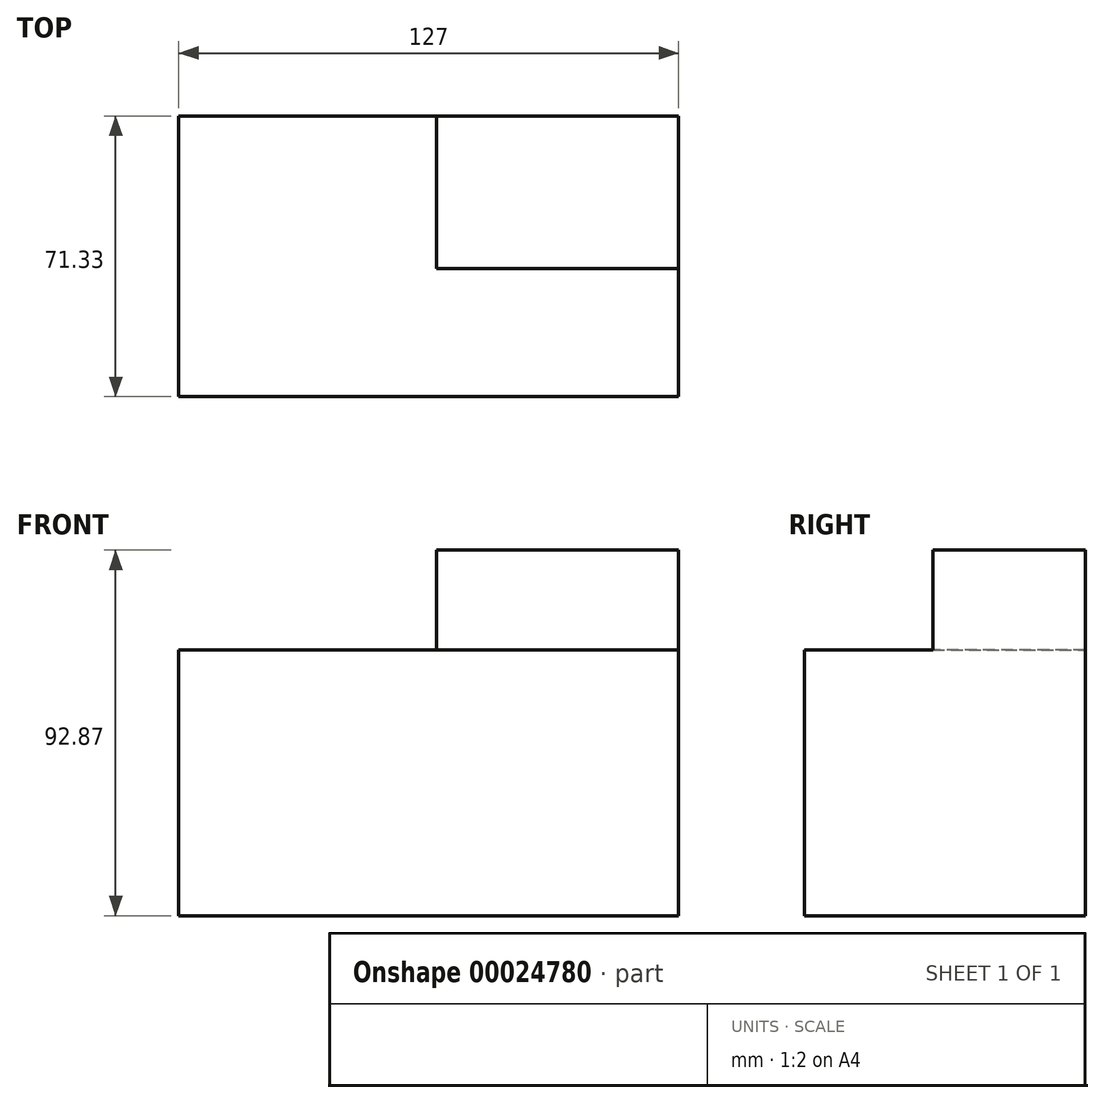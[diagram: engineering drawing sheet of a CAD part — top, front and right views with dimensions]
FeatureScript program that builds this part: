
annotation { "Feature Type Name" : "Feature", "Feature Type Description" : "" }
export const myFeature = defineFeature(function(context is Context, id is Id, definition is map)
    precondition{}
    {
        {
            var Q0;
            Q0=qCreatedBy(makeId("Right.planeOp"),FACE);
            var sketch = newSketch(context, id + "F0", { "sketchPlane" : qUnion([Q0])});
            skLineSegment(sketch, "E0.bottom", {"start": v(0, 0) * mm, "end": v(-71.33, 0) * mm});
            skLineSegment(sketch, "E0.top", {"start": v(0, 67.47) * mm, "end": v(-71.33, 67.47) * mm});
            skLineSegment(sketch, "E0.left", {"start": v(0, 0) * mm, "end": v(0, 67.47) * mm});
            skLineSegment(sketch, "E0.right", {"start": v(-71.33, 0) * mm, "end": v(-71.33, 67.47) * mm});
            skSolve(sketch);
        }
        {
            var Q0;
            Q0=makeQuery(id+"F0.imprint","IMPRINT",FACE,{"disambiguationData":[TD([[makeQuery(id+"F0.imprint","IMPRINT",EDGE,{"derivedFrom":sQuery(id+"F0.wireOp",EDGE,"E0.bottom")}),-1.0]])]});
            extrude(context, id + "F1", {"entities" : qUnion([Q0]), "depth" : 127 * mm});
        }
        {
            var Q0;
            Q0=makeQuery(id+"F1.opExtrude","SWEPT_FACE",FACE,{"disambiguationData":[OSD([sQuery(id+"F0.wireOp",EDGE,"E0.top")])]});
            var sketch = newSketch(context, id + "F2", { "sketchPlane" : qUnion([Q0])});
            skLineSegment(sketch, "E1.bottom", {"start": v(65.5, -38.76) * mm, "end": v(127, -38.76) * mm});
            skLineSegment(sketch, "E1.top", {"start": v(65.5, 0) * mm, "end": v(127, 0) * mm});
            skLineSegment(sketch, "E1.left", {"start": v(65.5, -38.76) * mm, "end": v(65.5, 0) * mm});
            skLineSegment(sketch, "E1.right", {"start": v(127, -38.76) * mm, "end": v(127, 0) * mm});
            skSolve(sketch);
        }
        {
            var Q0;
            Q0=makeQuery(id+"F2.imprint","IMPRINT",FACE,{"disambiguationData":[TD([[makeQuery(id+"F2.imprint","IMPRINT",EDGE,{"derivedFrom":sQuery(id+"F2.wireOp",EDGE,"E1.bottom")}),1.0]])]});
            extrude(context, id + "F3", {"entities" : qUnion([Q0]), "operationType" : NewBodyOperationType.ADD, "depth" : 25.4 * mm});
        }
    });
